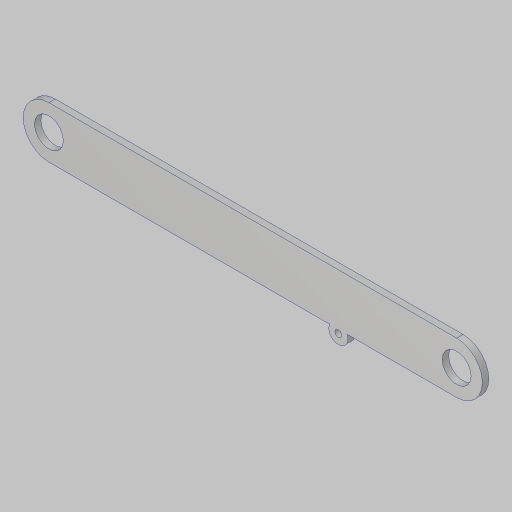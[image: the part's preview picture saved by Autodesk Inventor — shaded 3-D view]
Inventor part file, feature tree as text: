
AUTODESK INVENTOR PART (.ipt)
format: ipt  version: 2023.5 (Build 275446000, 446)  size: 108,032 bytes
history: native  units: in
note: dims shown in document units (in); Inventor stores cm internally (conversion verified against a paired STEP export)
features: sketch x1, extrude x1, hole x1
ambient origin geometry x8: Origin, YZ Plane, XZ Plane, XY Plane, X Axis, Y Axis, Z Axis, Center Point
bodies: Solid1 (feature_tree)
feature tree (3):
  sketch  "Sketch1"  dims[d0=1.125in d1=15.85in d2=2.0in d3=11.25in d5=0.25in d6=0.0in d7=0.266in d8=0.75in d9=0.507in d10=0.25in d11=0.5635in d12=1.0in d13=0.8108in d15=1.147in d16=0.75in]
  extrude  "Extrusion1"  Depth=15.85in
  hole  "Hole1"  [1 undecoded]
note: 1 required parameter value undecoded (feature->parameter linkage not recoverable at this tier; creation-order binding heuristic only, values carry confidence <= 0.55)
